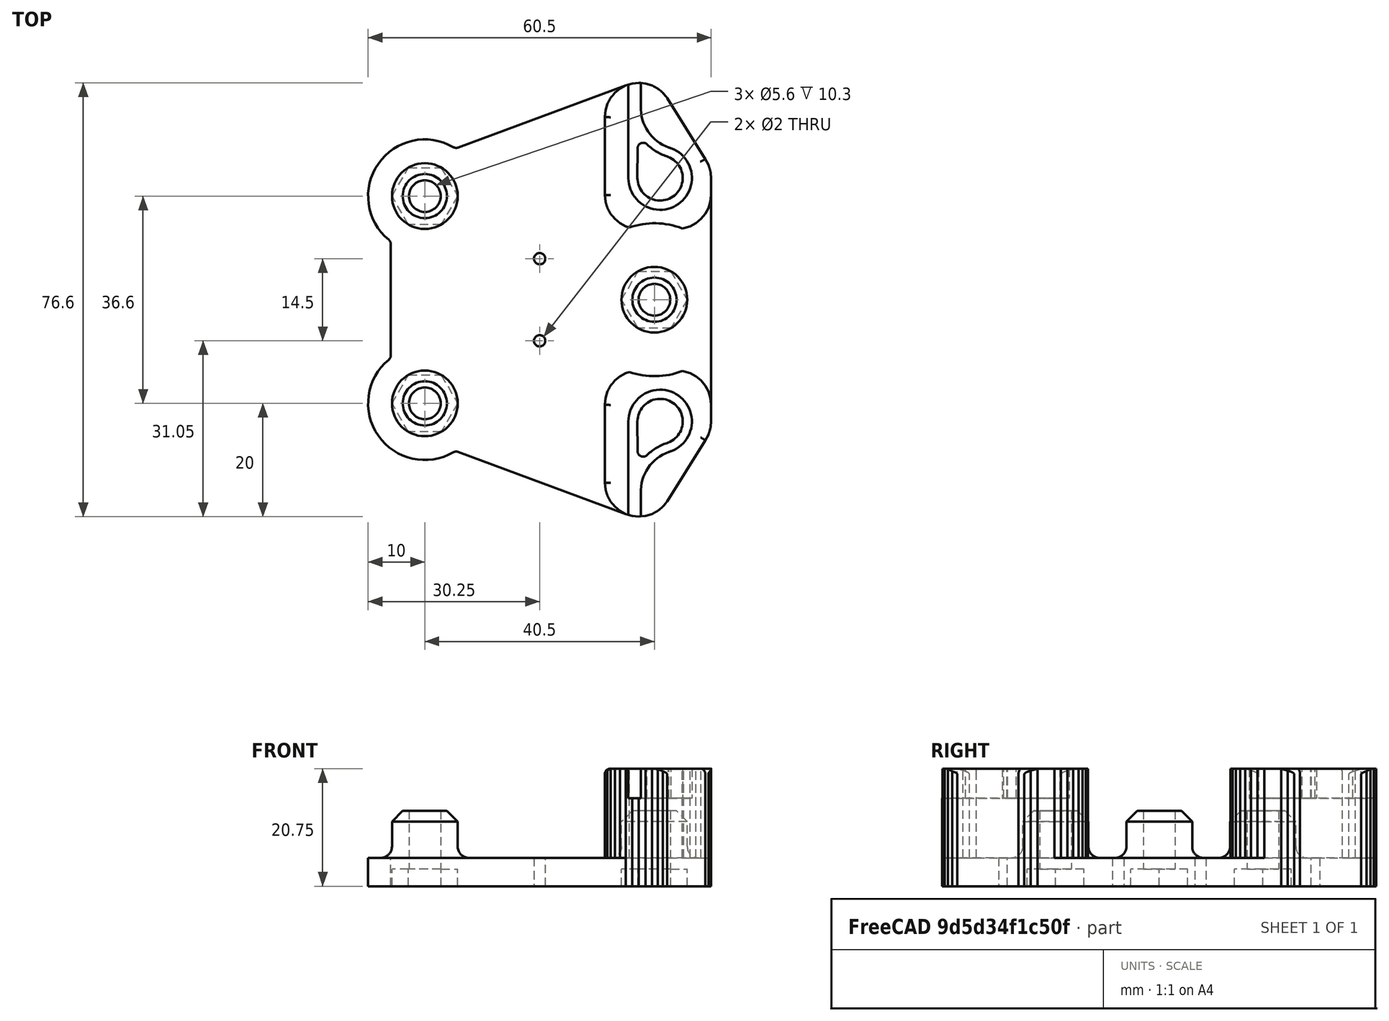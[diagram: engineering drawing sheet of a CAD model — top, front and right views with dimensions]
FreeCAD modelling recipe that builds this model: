
FCSTD DOCUMENT  (FreeCAD 0.19R24267 +99 (Git))
Label: carroX_V0
License: All rights reserved
LicenseURL: http://en.wikipedia.org/wiki/All_rights_reserved
objects: Part::Feature×137, Part::Part2DObjectPython×10, Part::FeaturePython×8, Part::Fillet×8, Part::Cylinder×7, Part::Cut×6, Part::MultiFuse×5, Part::Extrusion×5, Part::Prism×3, Part::Chamfer×3, Part::Fuse×1, App::DocumentObjectGroupPython×1, Part::Mirroring×1, Part::Refine×1
note: 195 computed .brp shape members not serialized (recipe doc carries the construction recipe); baked Part::Feature solids carry a one-line shape summary decoded from their .brp

FEATURE [Part::Feature] polygon
  shape: bbox 44.5 x 64.6 x 2e-07 mm, 1 faces, 0 solids (baked)
FEATURE [Part::Part2DObjectPython] circle  # Draft 2D object (typed FeaturePython)
  Area = 113.097
  FirstAngle = 0
  LastAngle = 0
  MakeFace = true
  Radius = 6
FEATURE [Part::FeaturePython] minkowski  # WARN: FeaturePython — macro-defined, semantics opaque (R4)
  Arguments = {'convexity': '0'}
  Children = -> [polygon,circle]
  Operation = minkowski
FEATURE [Part::Part2DObjectPython] circle001  # Draft 2D object (typed FeaturePython)
  Area = 314.159
  FirstAngle = 0
  LastAngle = 0
  MakeFace = true
  Placement = pos=(-20.25,-18.3,0) rot=(0,0,1;0rad)
  Radius = 10
FEATURE [Part::Part2DObjectPython] circle002  # Draft 2D object (typed FeaturePython)
  Area = 314.159
  FirstAngle = 0
  LastAngle = 0
  MakeFace = true
  Placement = pos=(-20.25,18.3,0) rot=(0,0,1;0rad)
  Radius = 10
FEATURE [Part::MultiFuse] union
  Shapes = -> [minkowski,circle001,circle002]
FEATURE [Part::Part2DObjectPython] circle003  # Draft 2D object (typed FeaturePython)
  Area = 24.6301
  FirstAngle = 0
  LastAngle = 0
  MakeFace = true
  Placement = pos=(-20.25,-18.3,0) rot=(0,0,1;0rad)
  Radius = 2.8
FEATURE [Part::Part2DObjectPython] circle004  # Draft 2D object (typed FeaturePython)
  Area = 24.6301
  FirstAngle = 0
  LastAngle = 0
  MakeFace = true
  Placement = pos=(20.25,0,0) rot=(0,0,1;0rad)
  Radius = 2.8
FEATURE [Part::Part2DObjectPython] circle005  # Draft 2D object (typed FeaturePython)
  Area = 24.6301
  FirstAngle = 0
  LastAngle = 0
  MakeFace = true
  Placement = pos=(-20.25,18.3,0) rot=(0,0,1;0rad)
  Radius = 2.8
FEATURE [Part::Part2DObjectPython] circle006  # Draft 2D object (typed FeaturePython)
  Area = 3.14159
  FirstAngle = 0
  LastAngle = 0
  MakeFace = true
  Placement = pos=(0,7.25,0) rot=(0,0,1;0rad)
  Radius = 1
FEATURE [Part::Part2DObjectPython] circle007  # Draft 2D object (typed FeaturePython)
  Area = 3.14159
  FirstAngle = 0
  LastAngle = 0
  MakeFace = true
  Placement = pos=(0,-7.25,0) rot=(0,0,1;0rad)
  Radius = 1
FEATURE [Part::MultiFuse] union001
  Shapes = -> [circle003,circle004,circle005,circle006,circle007]
FEATURE [Part::Cut] difference
  Base = -> union
  Tool = -> union001
FEATURE [Part::FeaturePython] RefineLinearExtrude  # WARN: FeaturePython — macro-defined, semantics opaque (R4)
  Base = -> difference
FEATURE [Part::Extrusion] LinearExtrude
  Base = -> RefineLinearExtrude
  Dir = (0,0,5)
  DirMode = 0
  FaceMakerClass = Part::FaceMakerBullseye
  LengthFwd = 0
  LengthRev = 0
  Solid = false
  Symmetric = false
FEATURE [Part::Feature] polygon001
  shape: bbox 6.75 x 13.8 x 2e-07 mm, 1 faces, 0 solids (baked)
FEATURE [Part::Part2DObjectPython] circle008  # Draft 2D object (typed FeaturePython)
  Area = 113.097
  FirstAngle = 0
  LastAngle = 0
  MakeFace = true
  Radius = 6
FEATURE [Part::FeaturePython] minkowski001  # WARN: FeaturePython — macro-defined, semantics opaque (R4)
  Arguments = {'convexity': '0'}
  Children = -> [polygon001,circle008]
  Operation = minkowski
FEATURE [Part::FeaturePython] RefineLinearExtrude001  # WARN: FeaturePython — macro-defined, semantics opaque (R4)
  Base = -> minkowski001
FEATURE [Part::Extrusion] LinearExtrude001
  Base = -> RefineLinearExtrude001
  Dir = (0,0,20.75)
  DirMode = 0
  FaceMakerClass = Part::FaceMakerBullseye
  LengthFwd = 0
  LengthRev = 0
  Solid = false
  Symmetric = false
FEATURE [Part::Feature] polygon002
  shape: bbox 6.75 x 13.8 x 2e-07 mm, 1 faces, 0 solids (baked)
FEATURE [Part::Part2DObjectPython] circle009  # Draft 2D object (typed FeaturePython)
  Area = 113.097
  FirstAngle = 0
  LastAngle = 0
  MakeFace = true
  Radius = 6
FEATURE [Part::FeaturePython] minkowski002  # WARN: FeaturePython — macro-defined, semantics opaque (R4)
  Arguments = {'convexity': '0'}
  Children = -> [polygon002,circle009]
  Operation = minkowski
FEATURE [Part::FeaturePython] RefineLinearExtrude002  # WARN: FeaturePython — macro-defined, semantics opaque (R4)
  Base = -> minkowski002
FEATURE [Part::Extrusion] LinearExtrude002
  Base = -> RefineLinearExtrude002
  Dir = (0,0,20.75)
  DirMode = 0
  FaceMakerClass = Part::FaceMakerBullseye
  LengthFwd = 0
  LengthRev = 0
  Solid = false
  Symmetric = false
FEATURE [Part::Fuse] union002
  Base = -> LinearExtrude001
  Tool = -> LinearExtrude002
FEATURE [Part::Cylinder] cylinder
  Angle = 360
  AttacherType = Attacher::AttachEngine3D
  Height = 60
  Placement = pos=(20.25,0,0) rot=(0,0,1;0rad)
  Radius = 13.5
FEATURE [Part::Cut] difference001
  Base = -> union002
  Tool = -> cylinder
FEATURE [Part::Cylinder] cylinder001
  Angle = 360
  AttacherType = Attacher::AttachEngine3D
  Height = 13.3
  Radius = 5.8
FEATURE [Part::Cylinder] cylinder002
  Angle = 360
  AttacherType = Attacher::AttachEngine3D
  Height = 53.2
  Placement = pos=(0,0,-26.6) rot=(0,0,1;0rad)
  Radius = 2.8
FEATURE [Part::Cut] difference002
  Base = -> cylinder001
  Placement = pos=(-20.25,-18.3,0) rot=(0,0,1;0rad)
  Tool = -> cylinder002
FEATURE [Part::Cylinder] cylinder003
  Angle = 360
  AttacherType = Attacher::AttachEngine3D
  Height = 13.3
  Radius = 5.8
FEATURE [Part::Cylinder] cylinder004
  Angle = 360
  AttacherType = Attacher::AttachEngine3D
  Height = 53.2
  Placement = pos=(0,0,-26.6) rot=(0,0,1;0rad)
  Radius = 2.8
FEATURE [Part::Cut] difference003
  Base = -> cylinder003
  Placement = pos=(-20.25,18.3,0) rot=(0,0,1;0rad)
  Tool = -> cylinder004
FEATURE [Part::Cylinder] cylinder005
  Angle = 360
  AttacherType = Attacher::AttachEngine3D
  Height = 13.3
  Radius = 5.8
FEATURE [Part::Cylinder] cylinder006
  Angle = 360
  AttacherType = Attacher::AttachEngine3D
  Height = 53.2
  Placement = pos=(0,0,-26.6) rot=(0,0,1;0rad)
  Radius = 2.8
FEATURE [Part::Cut] difference004
  Base = -> cylinder005
  Placement = pos=(20.25,0,0) rot=(0,0,1;0rad)
  Tool = -> cylinder006
FEATURE [Part::MultiFuse] union003
  Shapes = -> [LinearExtrude,difference001,difference002,difference003,difference004]
FEATURE [Part::Prism] prism
  AttacherType = Attacher::AttachEngine3D
  Circumradius = 5.79
  FirstAngle = 0
  Height = 6
  Placement = pos=(-20.25,-18.3,-3) rot=(0,0,1;0rad)
  Polygon = 6
  SecondAngle = 0
FEATURE [Part::Prism] prism001
  AttacherType = Attacher::AttachEngine3D
  Circumradius = 5.79
  FirstAngle = 0
  Height = 6
  Placement = pos=(-20.25,18.3,-3) rot=(0,0,1;0rad)
  Polygon = 6
  SecondAngle = 0
FEATURE [Part::Prism] prism002
  AttacherType = Attacher::AttachEngine3D
  Circumradius = 5.79
  FirstAngle = 0
  Height = 6
  Placement = pos=(20.25,0,-3) rot=(0,0,1;0rad)
  Polygon = 6
  SecondAngle = 0
FEATURE [Part::MultiFuse] Group
  Shapes = -> [prism,prism001,prism002]
FEATURE [App::DocumentObjectGroupPython] LayerContainer  label="Capas"  # scripted group (container) (typed FeaturePython)
FEATURE [Part::Feature] Line
  shape: bbox 25.93 x 2e-07 x 2e-07 mm, 0 faces, 0 solids (baked)
FEATURE [Part::Feature] Line001
  shape: bbox 5.23 x 0.01028 x 2e-07 mm, 0 faces, 0 solids (baked)
FEATURE [Part::Feature] Line002
  shape: bbox 13.12 x 2e-07 x 2e-07 mm, 0 faces, 0 solids (baked)
FEATURE [Part::Feature] Line003
  shape: bbox 46.78 x 2e-07 x 2e-07 mm, 0 faces, 0 solids (baked)
FEATURE [Part::Feature] Line004
  shape: bbox 46.66 x 2e-07 x 2e-07 mm, 0 faces, 0 solids (baked)
FEATURE [Part::Feature] Line005
  shape: bbox 2e-07 x 2.2 x 2e-07 mm, 0 faces, 0 solids (baked)
FEATURE [Part::Feature] Arc
  shape: bbox 7.844 x 7.989 x 2e-07 mm, 0 faces, 0 solids (baked)
FEATURE [Part::Feature] Arc001
  shape: bbox 0.9979 x 1.743 x 2e-07 mm, 0 faces, 0 solids (baked)
FEATURE [Part::Feature] Arc002
  shape: bbox 10.99 x 11.2 x 2e-07 mm, 0 faces, 0 solids (baked)
FEATURE [Part::Feature] Arc003
  shape: bbox 2.238 x 3.76 x 2e-07 mm, 0 faces, 0 solids (baked)
FEATURE [Part::Feature] Arc004
  shape: bbox 7.439 x 5.334 x 2e-07 mm, 0 faces, 0 solids (baked)
FEATURE [Part::Feature] dxf_ToyRepCart_all
  Placement = pos=(0,0,0) rot=(0,0,1;1.5708rad)
  shape: bbox 11.2 x 78.19 x 2e-07 mm, 1 faces, 0 solids (baked)
FEATURE [Part::FeaturePython] RefineLinearExtrude003  # WARN: FeaturePython — macro-defined, semantics opaque (R4)
  Base = -> dxf_ToyRepCart_all
FEATURE [Part::Extrusion] LinearExtrude003
  Base = -> RefineLinearExtrude003
  Dir = (0,0,100)
  DirMode = 0
  FaceMakerClass = Part::FaceMakerBullseye
  LengthFwd = 0
  LengthRev = 0
  Placement = pos=(21.25,-21.5,15.55) rot=(0,0,1;0rad)
  Solid = false
  Symmetric = false
FEATURE [Part::Feature] Line006
  shape: bbox 25.93 x 2e-07 x 2e-07 mm, 0 faces, 0 solids (baked)
FEATURE [Part::Feature] Line007
  shape: bbox 5.23 x 0.01028 x 2e-07 mm, 0 faces, 0 solids (baked)
FEATURE [Part::Feature] Line008
  shape: bbox 13.12 x 2e-07 x 2e-07 mm, 0 faces, 0 solids (baked)
FEATURE [Part::Feature] Line009
  shape: bbox 46.78 x 2e-07 x 2e-07 mm, 0 faces, 0 solids (baked)
FEATURE [Part::Feature] Line010
  shape: bbox 46.66 x 2e-07 x 2e-07 mm, 0 faces, 0 solids (baked)
FEATURE [Part::Feature] Line011
  shape: bbox 2e-07 x 2.2 x 2e-07 mm, 0 faces, 0 solids (baked)
FEATURE [Part::Feature] Arc005
  shape: bbox 7.844 x 7.989 x 2e-07 mm, 0 faces, 0 solids (baked)
FEATURE [Part::Feature] Arc006
  shape: bbox 0.9979 x 1.743 x 2e-07 mm, 0 faces, 0 solids (baked)
FEATURE [Part::Feature] Arc007
  shape: bbox 10.99 x 11.2 x 2e-07 mm, 0 faces, 0 solids (baked)
FEATURE [Part::Feature] Arc008
  shape: bbox 2.238 x 3.76 x 2e-07 mm, 0 faces, 0 solids (baked)
FEATURE [Part::Feature] Arc009
  shape: bbox 7.439 x 5.334 x 2e-07 mm, 0 faces, 0 solids (baked)
FEATURE [Part::Feature] dxf_ToyRepCart_all001
  Placement = pos=(0,0,0) rot=(0,0,1;1.5708rad)
  shape: bbox 11.2 x 78.19 x 2e-07 mm, 1 faces, 0 solids (baked)
FEATURE [Part::FeaturePython] RefineLinearExtrude004  # WARN: FeaturePython — macro-defined, semantics opaque (R4)
  Base = -> dxf_ToyRepCart_all001
FEATURE [Part::Extrusion] LinearExtrude004
  Base = -> RefineLinearExtrude004
  Dir = (0,0,100)
  DirMode = 0
  FaceMakerClass = Part::FaceMakerBullseye
  LengthFwd = 0
  LengthRev = 0
  Placement = pos=(21.25,-21.5,15.55) rot=(0,0,1;0rad)
  Solid = false
  Symmetric = false
FEATURE [Part::Mirroring] mirr_LinearExtrude004  label="mirrored LinearExtrude004"
  Base = (0,0,0)
  Normal = (0,1,0)
  Source = -> LinearExtrude004
FEATURE [Part::MultiFuse] union004
  Shapes = -> [Group,LinearExtrude003,mirr_LinearExtrude004]
FEATURE [Part::Cut] difference005
  Base = -> union003
  Tool = -> union004
FEATURE [Part::Feature] Line012
  shape: bbox 1.171 x 0.1152 x 2e-07 mm, 0 faces, 0 solids (baked)
FEATURE [Part::Feature] Line013
  shape: bbox 1.171 x 0.1152 x 2e-07 mm, 0 faces, 0 solids (baked)
FEATURE [Part::Feature] Line014
  shape: bbox 1.125 x 0.3418 x 2e-07 mm, 0 faces, 0 solids (baked)
FEATURE [Part::Feature] Line015
  shape: bbox 37.75 x 14 x 2e-07 mm, 0 faces, 0 solids (baked)
FEATURE [Part::Feature] Line016
  shape: bbox 1.037 x 0.5537 x 2e-07 mm, 0 faces, 0 solids (baked)
FEATURE [Part::Feature] Line017
  shape: bbox 0.9092 x 0.7471 x 2e-07 mm, 0 faces, 0 solids (baked)
FEATURE [Part::Feature] Line018
  shape: bbox 0.7471 x 0.9092 x 2e-07 mm, 0 faces, 0 solids (baked)
FEATURE [Part::Feature] Line019
  shape: bbox 0.5537 x 1.037 x 2e-07 mm, 0 faces, 0 solids (baked)
FEATURE [Part::Feature] Line020
  shape: bbox 0.3418 x 1.125 x 2e-07 mm, 0 faces, 0 solids (baked)
FEATURE [Part::Feature] Line021
  shape: bbox 0.1152 x 1.171 x 2e-07 mm, 0 faces, 0 solids (baked)
FEATURE [Part::Feature] Line022
  shape: bbox 2e-07 x 36.6 x 2e-07 mm, 0 faces, 0 solids (baked)
FEATURE [Part::Feature] Line023
  shape: bbox 0.1152 x 1.171 x 2e-07 mm, 0 faces, 0 solids (baked)
FEATURE [Part::Feature] Line024
  shape: bbox 0.3418 x 1.125 x 2e-07 mm, 0 faces, 0 solids (baked)
FEATURE [Part::Feature] Line025
  shape: bbox 0.5537 x 1.037 x 2e-07 mm, 0 faces, 0 solids (baked)
FEATURE [Part::Feature] Line026
  shape: bbox 0.7471 x 0.9092 x 2e-07 mm, 0 faces, 0 solids (baked)
FEATURE [Part::Feature] Line027
  shape: bbox 0.9092 x 0.7471 x 2e-07 mm, 0 faces, 0 solids (baked)
FEATURE [Part::Feature] Line028
  shape: bbox 1.037 x 0.5537 x 2e-07 mm, 0 faces, 0 solids (baked)
FEATURE [Part::Feature] Line029
  shape: bbox 37.75 x 14 x 2e-07 mm, 0 faces, 0 solids (baked)
FEATURE [Part::Feature] Line030
  shape: bbox 1.125 x 0.3418 x 2e-07 mm, 0 faces, 0 solids (baked)
FEATURE [Part::Feature] Line031
  shape: bbox 1.171 x 0.1152 x 2e-07 mm, 0 faces, 0 solids (baked)
FEATURE [Part::Feature] Line032
  shape: bbox 1.171 x 0.1152 x 2e-07 mm, 0 faces, 0 solids (baked)
FEATURE [Part::Feature] Line033
  shape: bbox 1.125 x 0.3418 x 2e-07 mm, 0 faces, 0 solids (baked)
FEATURE [Part::Feature] Line034
  shape: bbox 1.037 x 0.5537 x 2e-07 mm, 0 faces, 0 solids (baked)
FEATURE [Part::Feature] Line035
  shape: bbox 0.9092 x 0.7471 x 2e-07 mm, 0 faces, 0 solids (baked)
FEATURE [Part::Feature] Line036
  shape: bbox 0.7471 x 0.9092 x 2e-07 mm, 0 faces, 0 solids (baked)
FEATURE [Part::Feature] Line037
  shape: bbox 6.75 x 10.8 x 2e-07 mm, 0 faces, 0 solids (baked)
FEATURE [Part::Feature] Line038
  shape: bbox 0.5537 x 1.037 x 2e-07 mm, 0 faces, 0 solids (baked)
FEATURE [Part::Feature] Line039
  shape: bbox 0.3418 x 1.125 x 2e-07 mm, 0 faces, 0 solids (baked)
FEATURE [Part::Feature] Line040
  shape: bbox 0.1152 x 1.171 x 2e-07 mm, 0 faces, 0 solids (baked)
FEATURE [Part::Feature] Line041
  shape: bbox 2e-07 x 43 x 2e-07 mm, 0 faces, 0 solids (baked)
FEATURE [Part::Feature] Line042
  shape: bbox 0.1152 x 1.171 x 2e-07 mm, 0 faces, 0 solids (baked)
FEATURE [Part::Feature] Line043
  shape: bbox 0.3418 x 1.125 x 2e-07 mm, 0 faces, 0 solids (baked)
FEATURE [Part::Feature] Line044
  shape: bbox 0.5537 x 1.037 x 2e-07 mm, 0 faces, 0 solids (baked)
FEATURE [Part::Feature] Line045
  shape: bbox 6.75 x 10.8 x 2e-07 mm, 0 faces, 0 solids (baked)
FEATURE [Part::Feature] Line046
  shape: bbox 0.7471 x 0.9092 x 2e-07 mm, 0 faces, 0 solids (baked)
FEATURE [Part::Feature] Line047
  shape: bbox 0.9092 x 0.7471 x 2e-07 mm, 0 faces, 0 solids (baked)
FEATURE [Part::Feature] Line048
  shape: bbox 1.037 x 0.5537 x 2e-07 mm, 0 faces, 0 solids (baked)
FEATURE [Part::Feature] Line049
  shape: bbox 1.125 x 0.3418 x 2e-07 mm, 0 faces, 0 solids (baked)
FEATURE [Part::Feature] Line050
  shape: bbox 1.125 x 0.3418 x 2e-07 mm, 0 faces, 0 solids (baked)
FEATURE [Part::Feature] Line051
  shape: bbox 1.171 x 0.1152 x 2e-07 mm, 0 faces, 0 solids (baked)
FEATURE [Part::Feature] Line052
  shape: bbox 1.171 x 0.1152 x 2e-07 mm, 0 faces, 0 solids (baked)
FEATURE [Part::Feature] Line053
  shape: bbox 1.125 x 0.3418 x 2e-07 mm, 0 faces, 0 solids (baked)
FEATURE [Part::Feature] Line054
  shape: bbox 1.037 x 0.5537 x 2e-07 mm, 0 faces, 0 solids (baked)
FEATURE [Part::Feature] Line055
  shape: bbox 0.9092 x 0.7471 x 2e-07 mm, 0 faces, 0 solids (baked)
FEATURE [Part::Feature] Line056
  shape: bbox 0.7471 x 0.9092 x 2e-07 mm, 0 faces, 0 solids (baked)
FEATURE [Part::Feature] Line057
  shape: bbox 0.5537 x 1.037 x 2e-07 mm, 0 faces, 0 solids (baked)
FEATURE [Part::Feature] Line058
  shape: bbox 0.3418 x 1.125 x 2e-07 mm, 0 faces, 0 solids (baked)
FEATURE [Part::Feature] Line059
  shape: bbox 0.1152 x 1.171 x 2e-07 mm, 0 faces, 0 solids (baked)
FEATURE [Part::Feature] Line060
  shape: bbox 2e-07 x 13.8 x 2e-07 mm, 0 faces, 0 solids (baked)
FEATURE [Part::Feature] Line061
  shape: bbox 0.1152 x 1.171 x 2e-07 mm, 0 faces, 0 solids (baked)
FEATURE [Part::Feature] Line062
  shape: bbox 0.3418 x 1.125 x 2e-07 mm, 0 faces, 0 solids (baked)
FEATURE [Part::Feature] Line063
  shape: bbox 0.5537 x 1.037 x 2e-07 mm, 0 faces, 0 solids (baked)
FEATURE [Part::Feature] Line064
  shape: bbox 0.7471 x 0.9092 x 2e-07 mm, 0 faces, 0 solids (baked)
FEATURE [Part::Feature] Line065
  shape: bbox 0.9092 x 0.7471 x 2e-07 mm, 0 faces, 0 solids (baked)
FEATURE [Part::Feature] Line066
  shape: bbox 1.037 x 0.5537 x 2e-07 mm, 0 faces, 0 solids (baked)
FEATURE [Part::Feature] Line067
  shape: bbox 1.125 x 0.3418 x 2e-07 mm, 0 faces, 0 solids (baked)
FEATURE [Part::Feature] Line068
  shape: bbox 1.171 x 0.1152 x 2e-07 mm, 0 faces, 0 solids (baked)
FEATURE [Part::Feature] Line069
  shape: bbox 6.75 x 2e-07 x 2e-07 mm, 0 faces, 0 solids (baked)
FEATURE [Part::Feature] Line070
  shape: bbox 1.171 x 0.1152 x 2e-07 mm, 0 faces, 0 solids (baked)
FEATURE [Part::Feature] Line071
  shape: bbox 1.125 x 0.3418 x 2e-07 mm, 0 faces, 0 solids (baked)
FEATURE [Part::Feature] Line072
  shape: bbox 1.037 x 0.5537 x 2e-07 mm, 0 faces, 0 solids (baked)
FEATURE [Part::Feature] Line073
  shape: bbox 0.9092 x 0.7471 x 2e-07 mm, 0 faces, 0 solids (baked)
FEATURE [Part::Feature] Line074
  shape: bbox 0.7471 x 0.9092 x 2e-07 mm, 0 faces, 0 solids (baked)
FEATURE [Part::Feature] Line075
  shape: bbox 0.5537 x 1.037 x 2e-07 mm, 0 faces, 0 solids (baked)
FEATURE [Part::Feature] Line076
  shape: bbox 0.3418 x 1.125 x 2e-07 mm, 0 faces, 0 solids (baked)
FEATURE [Part::Feature] Line077
  shape: bbox 0.1152 x 1.171 x 2e-07 mm, 0 faces, 0 solids (baked)
FEATURE [Part::Feature] Line078
  shape: bbox 2e-07 x 3 x 2e-07 mm, 0 faces, 0 solids (baked)
FEATURE [Part::Feature] Line079
  shape: bbox 0.1152 x 1.171 x 2e-07 mm, 0 faces, 0 solids (baked)
FEATURE [Part::Feature] Line080
  shape: bbox 0.3418 x 1.125 x 2e-07 mm, 0 faces, 0 solids (baked)
FEATURE [Part::Feature] Line081
  shape: bbox 0.5537 x 1.037 x 2e-07 mm, 0 faces, 0 solids (baked)
FEATURE [Part::Feature] Line082
  shape: bbox 6.75 x 10.8 x 2e-07 mm, 0 faces, 0 solids (baked)
FEATURE [Part::Feature] Line083
  shape: bbox 0.7471 x 0.9092 x 2e-07 mm, 0 faces, 0 solids (baked)
FEATURE [Part::Feature] Line084
  shape: bbox 0.9092 x 0.7471 x 2e-07 mm, 0 faces, 0 solids (baked)
FEATURE [Part::Feature] Line085
  shape: bbox 1.037 x 0.5537 x 2e-07 mm, 0 faces, 0 solids (baked)
FEATURE [Part::Feature] Line086
  shape: bbox 0.7471 x 0.9092 x 2e-07 mm, 0 faces, 0 solids (baked)
FEATURE [Part::Feature] Line087
  shape: bbox 0.9092 x 0.7471 x 2e-07 mm, 0 faces, 0 solids (baked)
FEATURE [Part::Feature] Line088
  shape: bbox 1.037 x 0.5537 x 2e-07 mm, 0 faces, 0 solids (baked)
FEATURE [Part::Feature] Line089
  shape: bbox 1.125 x 0.3418 x 2e-07 mm, 0 faces, 0 solids (baked)
FEATURE [Part::Feature] Line090
  shape: bbox 1.171 x 0.1152 x 2e-07 mm, 0 faces, 0 solids (baked)
FEATURE [Part::Feature] Line091
  shape: bbox 6.75 x 2e-07 x 2e-07 mm, 0 faces, 0 solids (baked)
FEATURE [Part::Feature] Line092
  shape: bbox 1.171 x 0.1152 x 2e-07 mm, 0 faces, 0 solids (baked)
FEATURE [Part::Feature] Line093
  shape: bbox 1.125 x 0.3418 x 2e-07 mm, 0 faces, 0 solids (baked)
FEATURE [Part::Feature] Line094
  shape: bbox 1.037 x 0.5537 x 2e-07 mm, 0 faces, 0 solids (baked)
FEATURE [Part::Feature] Line095
  shape: bbox 0.9092 x 0.7471 x 2e-07 mm, 0 faces, 0 solids (baked)
FEATURE [Part::Feature] Line096
  shape: bbox 0.7471 x 0.9092 x 2e-07 mm, 0 faces, 0 solids (baked)
FEATURE [Part::Feature] Line097
  shape: bbox 0.5537 x 1.037 x 2e-07 mm, 0 faces, 0 solids (baked)
FEATURE [Part::Feature] Line098
  shape: bbox 0.3418 x 1.125 x 2e-07 mm, 0 faces, 0 solids (baked)
FEATURE [Part::Feature] Line099
  shape: bbox 0.1152 x 1.171 x 2e-07 mm, 0 faces, 0 solids (baked)
FEATURE [Part::Feature] Line100
  shape: bbox 2e-07 x 13.8 x 2e-07 mm, 0 faces, 0 solids (baked)
FEATURE [Part::Feature] Line101
  shape: bbox 0.1152 x 1.171 x 2e-07 mm, 0 faces, 0 solids (baked)
FEATURE [Part::Feature] Line102
  shape: bbox 0.3418 x 1.125 x 2e-07 mm, 0 faces, 0 solids (baked)
FEATURE [Part::Feature] Line103
  shape: bbox 0.5537 x 1.037 x 2e-07 mm, 0 faces, 0 solids (baked)
FEATURE [Part::Feature] Line104
  shape: bbox 0.7471 x 0.9092 x 2e-07 mm, 0 faces, 0 solids (baked)
FEATURE [Part::Feature] Line105
  shape: bbox 0.9092 x 0.7471 x 2e-07 mm, 0 faces, 0 solids (baked)
FEATURE [Part::Feature] Line106
  shape: bbox 1.037 x 0.5537 x 2e-07 mm, 0 faces, 0 solids (baked)
FEATURE [Part::Feature] Line107
  shape: bbox 1.125 x 0.3418 x 2e-07 mm, 0 faces, 0 solids (baked)
FEATURE [Part::Feature] Line108
  shape: bbox 1.171 x 0.1152 x 2e-07 mm, 0 faces, 0 solids (baked)
FEATURE [Part::Feature] Line109
  shape: bbox 1.171 x 0.1152 x 2e-07 mm, 0 faces, 0 solids (baked)
FEATURE [Part::Feature] Line110
  shape: bbox 1.125 x 0.3418 x 2e-07 mm, 0 faces, 0 solids (baked)
FEATURE [Part::Feature] Line111
  shape: bbox 1.037 x 0.5537 x 2e-07 mm, 0 faces, 0 solids (baked)
FEATURE [Part::Feature] Line112
  shape: bbox 0.9092 x 0.7471 x 2e-07 mm, 0 faces, 0 solids (baked)
FEATURE [Part::Feature] Line113
  shape: bbox 0.7471 x 0.9092 x 2e-07 mm, 0 faces, 0 solids (baked)
FEATURE [Part::Feature] Line114
  shape: bbox 6.75 x 10.8 x 2e-07 mm, 0 faces, 0 solids (baked)
FEATURE [Part::Feature] Line115
  shape: bbox 0.5537 x 1.037 x 2e-07 mm, 0 faces, 0 solids (baked)
FEATURE [Part::Feature] Line116
  shape: bbox 0.3418 x 1.125 x 2e-07 mm, 0 faces, 0 solids (baked)
FEATURE [Part::Feature] Line117
  shape: bbox 0.1152 x 1.171 x 2e-07 mm, 0 faces, 0 solids (baked)
FEATURE [Part::Feature] Line118
  shape: bbox 2e-07 x 3 x 2e-07 mm, 0 faces, 0 solids (baked)
FEATURE [Part::Feature] Line119
  shape: bbox 0.1152 x 1.171 x 2e-07 mm, 0 faces, 0 solids (baked)
FEATURE [Part::Feature] Line120
  shape: bbox 0.3418 x 1.125 x 2e-07 mm, 0 faces, 0 solids (baked)
FEATURE [Part::Feature] Line121
  shape: bbox 0.5537 x 1.037 x 2e-07 mm, 0 faces, 0 solids (baked)
FEATURE [Part::Refine] difference005001
  Source = -> difference005
FEATURE [Part::Fillet] Fillet
  Base = -> difference005001
  Edges = 1 edges r=2: [Edge348]
FEATURE [Part::Fillet] Fillet001
  Base = -> Fillet
  Edges = 1 edges r=2: [Edge54]
FEATURE [Part::Fillet] Fillet002
  Base = -> Fillet001
  Edges = 1 edges r=1: [Edge70]
FEATURE [Part::Fillet] Fillet003
  Base = -> Fillet002
  Edges = 1 edges r=1: [Edge61]
FEATURE [Part::Fillet] Fillet004
  Base = -> Fillet003
  Edges = 1 edges r=1: [Edge68]
FEATURE [Part::Fillet] Fillet005
  Base = -> Fillet004
  Edges = 1 edges r=2: [Edge58]
FEATURE [Part::Fillet] Fillet006
  Base = -> Fillet005
  Edges = 1 edges r=1: [Edge76]
FEATURE [Part::Chamfer] Chamfer
  Base = -> Fillet006
  Edges = 1 edges r=1.9: [Edge271]
FEATURE [Part::Chamfer] Chamfer001
  Base = -> Chamfer
  Edges = 1 edges r=1.9: [Edge282]
FEATURE [Part::Chamfer] Chamfer002
  Base = -> Chamfer001
  Edges = 1 edges r=1.9: [Edge284]
FEATURE [Part::Fillet] Fillet007
  Base = -> Chamfer002
  Edges = 4 edges r=1: [Edge91,Edge163,Edge250,Edge265]
